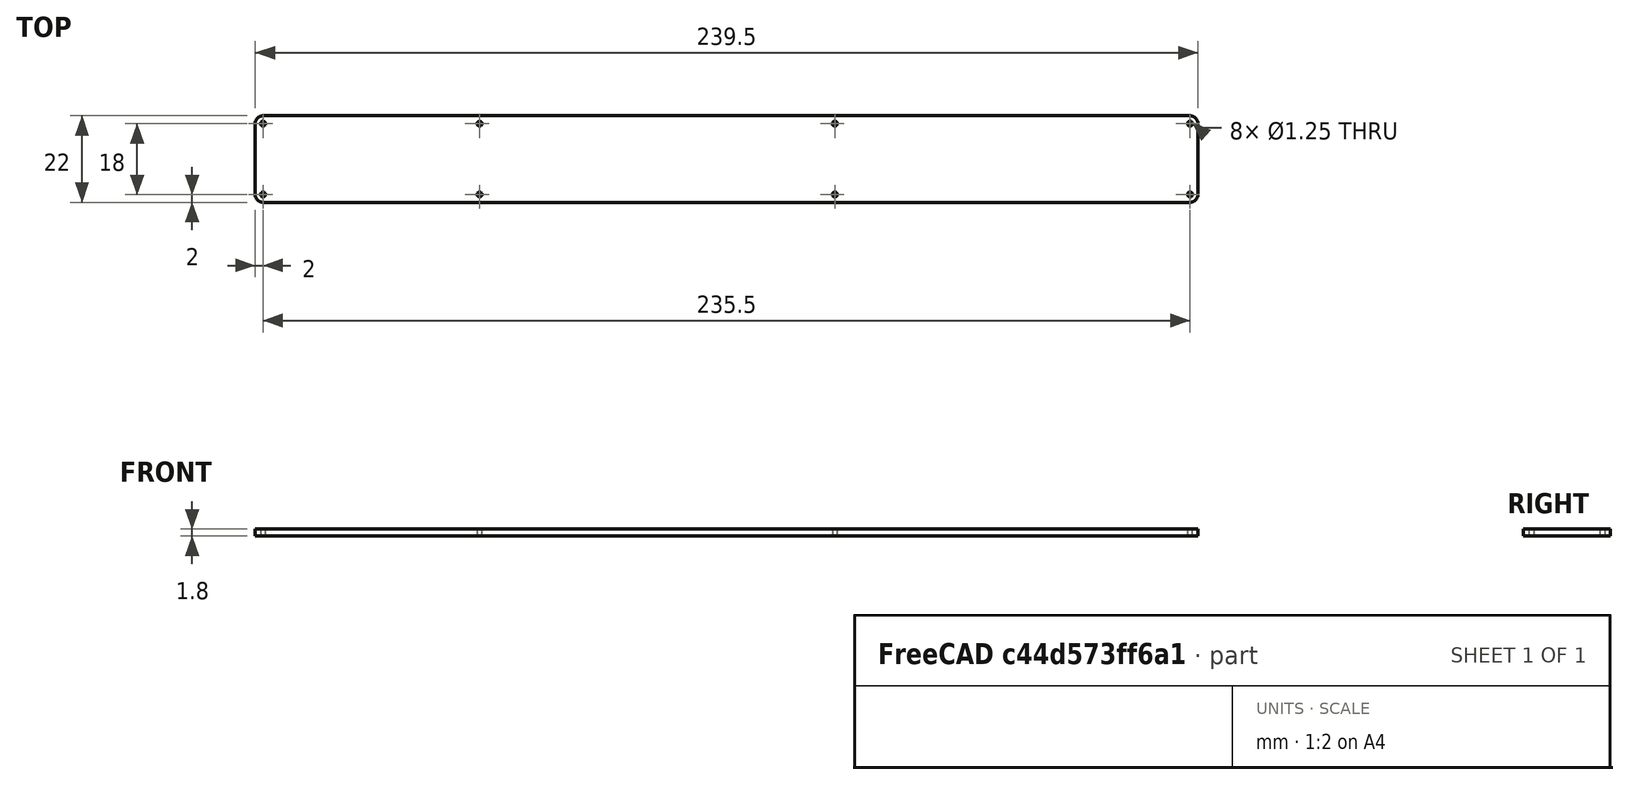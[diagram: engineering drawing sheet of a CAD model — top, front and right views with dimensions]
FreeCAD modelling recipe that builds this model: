
FCSTD DOCUMENT  (FreeCAD 1.0R39285 (Git))
Label: display-plate
License: All rights reserved
LicenseURL: https://en.wikipedia.org/wiki/All_rights_reserved
objects: Sketcher::SketchObject×1, PartDesign::Pad×1, PartDesign::Body×1
note: 6 computed .brp shape members not serialized (recipe doc carries the construction recipe); baked Part::Feature solids carry a one-line shape summary decoded from their .brp

FEATURE [Sketcher::SketchObject] Sketch
  ArcFitTolerance = 1e-06
  AttachmentSupport = -> [XY_Plane]
  FullyConstrained = true
  MakeInternals = false
  MapMode = 5
  sketch-geometry (20):
    g0: LineSegment StartX=-119.75 StartY=9 StartZ=0 EndX=-119.75 EndY=-9 EndZ=0
    g1: LineSegment StartX=-117.75 StartY=-11 StartZ=0 EndX=117.75 EndY=-11 EndZ=0
    g2: LineSegment StartX=119.75 StartY=-9 StartZ=0 EndX=119.75 EndY=9 EndZ=0
    g3: LineSegment StartX=117.75 StartY=11 StartZ=0 EndX=-117.75 EndY=11 EndZ=0
    g4: ArcOfCircle CenterX=117.75 CenterY=9 CenterZ=0 NormalX=0 NormalY=0 NormalZ=1 AngleXU=0 Radius=2 StartAngle=1e-16 EndAngle=1.5708
    g5: GeomPoint [constr] X=119.75 Y=11 Z=0
    g6: ArcOfCircle CenterX=117.75 CenterY=-9 CenterZ=0 NormalX=0 NormalY=0 NormalZ=1 AngleXU=0 Radius=2 StartAngle=4.71239 EndAngle=6.28319
    g7: GeomPoint [constr] X=119.75 Y=-11 Z=0
    g8: ArcOfCircle CenterX=-117.75 CenterY=-9 CenterZ=0 NormalX=0 NormalY=0 NormalZ=1 AngleXU=0 Radius=2 StartAngle=3.14159 EndAngle=4.71239
    g9: GeomPoint [constr] X=-119.75 Y=-11 Z=0
    g10: ArcOfCircle CenterX=-117.75 CenterY=9 CenterZ=0 NormalX=0 NormalY=0 NormalZ=1 AngleXU=0 Radius=2 StartAngle=1.5708 EndAngle=3.14159
    g11: GeomPoint [constr] X=-119.75 Y=11 Z=0
    g12: Circle CenterX=-117.75 CenterY=9 CenterZ=0 NormalX=0 NormalY=0 NormalZ=1 AngleXU=0 Radius=0.625
    g13: Circle CenterX=117.75 CenterY=9 CenterZ=0 NormalX=0 NormalY=0 NormalZ=1 AngleXU=0 Radius=0.625
    g14: Circle CenterX=-117.75 CenterY=-9 CenterZ=0 NormalX=0 NormalY=0 NormalZ=1 AngleXU=0 Radius=0.625
    g15: Circle CenterX=-62.75 CenterY=9 CenterZ=0 NormalX=0 NormalY=0 NormalZ=1 AngleXU=0 Radius=0.625
    g16: Circle CenterX=-62.75 CenterY=-9 CenterZ=0 NormalX=0 NormalY=0 NormalZ=1 AngleXU=0 Radius=0.625
    g17: Circle CenterX=27.5 CenterY=9 CenterZ=0 NormalX=0 NormalY=0 NormalZ=1 AngleXU=0 Radius=0.625
    g18: Circle CenterX=117.75 CenterY=-9 CenterZ=0 NormalX=0 NormalY=0 NormalZ=1 AngleXU=0 Radius=0.625
    g19: Circle CenterX=27.5 CenterY=-9 CenterZ=0 NormalX=0 NormalY=0 NormalZ=1 AngleXU=0 Radius=0.625
  constraints (49):
    c: Vertical(g0)
    c: Vertical(g2)
    c: Horizontal(g1)
    c: Horizontal(g3)
    c: DistanceY(g9,g11) = 22
    c: DistanceX(g11,g5) = 239.5
    c: Symmetric(g11,g7,g-1)
    c: PointOnObject(g5,g3)
    c: PointOnObject(g5,g2)
    c: Tangent(g3,g4) = -1.5708
    c: Tangent(g2,g4) = -1.5708
    c: PointOnObject(g7,g2)
    c: PointOnObject(g7,g1)
    c: Tangent(g2,g6) = -1.5708
    c: Tangent(g1,g6) = -1.5708
    c: PointOnObject(g9,g1)
    c: PointOnObject(g9,g0)
    c: Tangent(g1,g8) = -1.5708
    c: Tangent(g0,g8) = -1.5708
    c: PointOnObject(g11,g0)
    c: PointOnObject(g11,g3)
    c: Tangent(g0,g10) = -1.5708
    c: Tangent(g3,g10) = -1.5708
    c: Radius(g10) = 2
    c: Equal(g6,g4)
    c: Equal(g4,g8)
    c: Equal(g8,g10)
    c: Diameter(g12) = 1.25
    c: Coincident(g12,g10)
    c: Coincident(g13,g4)
    c: Equal(g12,g14)
    c: Equal(g15,g16)
    c: Equal(g12,g17)
    c: Equal(g17,g19)
    c: DistanceX(g10,g15) = 55
    c: DistanceY(g14,g10) = 18
    c: DistanceX(g15,g17) = 90.25
    c: Horizontal(g10,g15)
    c: Horizontal(g15,g17)
    c: Horizontal(g8,g16)
    c: Horizontal(g16,g19)
    c: Vertical(g15,g16)
    c: Vertical(g17,g19)
    c: Equal(g18,g13)
    c: Equal(g13,g16)
    c: Equal(g15,g12)
    c: Vertical(g18,g4)
    c: Vertical(g14,g10)
    c: Horizontal(g18,g19)
FEATURE [PartDesign::Pad] Pad
  Direction = (0,0,1)
  Length = 1.8
  Length2 = 10
  Profile = -> Sketch
  ReferenceAxis = -> Sketch [N_Axis]
  Refine = true
  Suppressed = false
  Type = 0
FEATURE [PartDesign::Body] Body
  AllowCompound = false
  Group = -> [Sketch,Pad]
  Origin = -> Origin
  Tip = -> Pad
